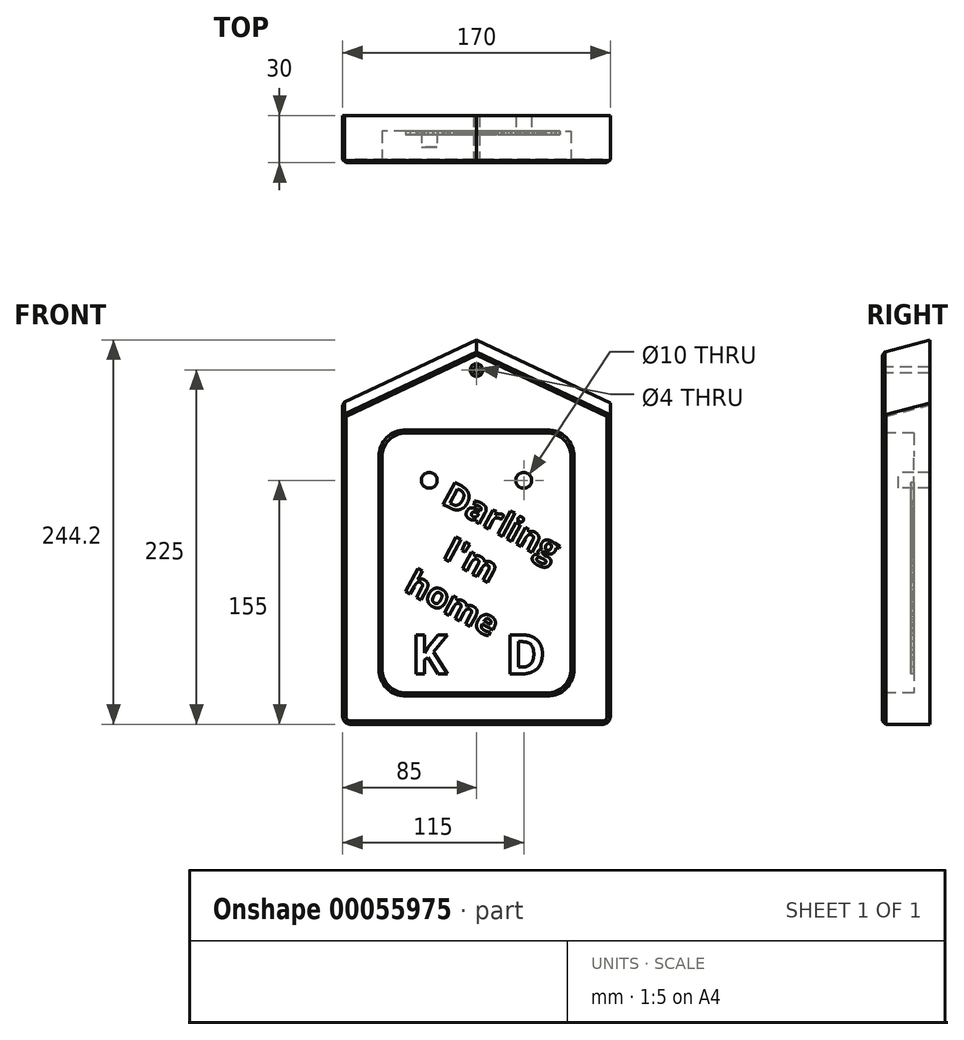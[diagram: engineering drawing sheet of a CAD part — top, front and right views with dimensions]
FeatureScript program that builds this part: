
annotation { "Feature Type Name" : "Feature", "Feature Type Description" : "" }
export const myFeature = defineFeature(function(context is Context, id is Id, definition is map)
    precondition{}
    {
        {
            var Q0;
            Q0=qCreatedBy(makeId("Front.planeOp"),FACE);
            var sketch = newSketch(context, id + "F0", { "sketchPlane" : qUnion([Q0])});
            skLineSegment(sketch, "E0.rect.bottom", {"start": v(45, -82.5) * mm, "end": v(-45, -82.5) * mm});
            skLineSegment(sketch, "E0.rect.top", {"start": v(45, 82.5) * mm, "end": v(-45, 82.5) * mm});
            skLineSegment(sketch, "E0.rect.left", {"start": v(60, -67.5) * mm, "end": v(60, 67.5) * mm});
            skLineSegment(sketch, "E0.rect.right", {"start": v(-60, -67.5) * mm, "end": v(-60, 67.5) * mm});
            skPoint(sketch, "E0.rect.middle", {"position": v(0, 0) * mm});
            skCircle(sketch, "E1", {"center": v(-30, 52.5) * mm, "radius": 5 * mm});
            skCircle(sketch, "E2.MirrorC", {"center": v(30, 52.5) * mm, "radius": 5 * mm});
            skPoint(sketch, "E3.visualSharp", {"position": v(60, 82.5) * mm});
            skArc(sketch, "E3.filletArc", {"start": v(60, 67.5) * mm, "mid": v(55.6, 78.1) * mm, "end": v(45, 82.5) * mm});
            skPoint(sketch, "E4.visualSharp", {"position": v(-60, 82.5) * mm});
            skArc(sketch, "E4.filletArc", {"start": v(-45, 82.5) * mm, "mid": v(-55.6, 78.1) * mm, "end": v(-60, 67.5) * mm});
            skPoint(sketch, "E5.visualSharp", {"position": v(-60, -82.5) * mm});
            skArc(sketch, "E5.filletArc", {"start": v(-60, -67.5) * mm, "mid": v(-55.6, -78.1) * mm, "end": v(-45, -82.5) * mm});
            skPoint(sketch, "E6.visualSharp", {"position": v(60, -82.5) * mm});
            skArc(sketch, "E6.filletArc", {"start": v(45, -82.5) * mm, "mid": v(55.6, -78.1) * mm, "end": v(60, -67.5) * mm});
            skLineSegment(sketch, "E7.rect.bottom", {"start": v(0, -102.5) * mm, "end": v(-80, -102.5) * mm});
            skLineSegment(sketch, "E7.rect.top", {"start": v(0, 142.5) * mm, "end": v(-85, 102.5) * mm});
            skLineSegment(sketch, "E7.rect.right", {"start": v(-85, -97.5) * mm, "end": v(-85, 102.5) * mm});
            skText(sketch, "E8", { "text": "K", "fontName": "OpenSans-Bold.ttf"});
            skText(sketch, "E9", { "text": "D", "fontName": "OpenSans-Bold.ttf"});
            skPoint(sketch, "E10.startSnap0", {"position": v(0, 142.5) * mm});
            skPoint(sketch, "E10.endSnap0", {"position": v(0, -82.5) * mm});
            skText(sketch, "E11", { "text": "Darling\n   I\'m\n home", "fontName": "OpenSans-Bold.ttf"});
            skPoint(sketch, "E12.visualSharp", {"position": v(-85, -102.5) * mm});
            skArc(sketch, "E12.filletArc", {"start": v(-85, -97.5) * mm, "mid": v(-83.54, -101.04) * mm, "end": v(-80, -102.5) * mm});
            skCircle(sketch, "E13", {"center": v(0, 122.5) * mm, "radius": 2 * mm});
            skPoint(sketch, "E14.MirrorCS.start.orphan", {"position": v(0, -102.5) * mm});
            skLineSegment(sketch, "E15", {"start": v(0, 105.13) * mm, "end": v(0, -95.47) * mm, "construction": true});
            skLineSegment(sketch, "E16.MirrorCS", {"start": v(0, 142.5) * mm, "end": v(85, 102.5) * mm});
            skLineSegment(sketch, "E17.MirrorCS", {"start": v(85, -97.5) * mm, "end": v(85, 102.5) * mm});
            skArc(sketch, "E18.MirrorCS", {"start": v(85, -97.5) * mm, "mid": v(83.54, -101.04) * mm, "end": v(80, -102.5) * mm});
            skLineSegment(sketch, "E19.MirrorCS", {"start": v(0, -102.5) * mm, "end": v(80, -102.5) * mm});
            const initialGuessF0  = {"E8": [-0.04153, -0.0705, 1, 0, 0.025], "E9": [0.01816, -0.0705, 1, 0, 0.025], "E11": [-0.02296, 0.03819, 0.87871, -0.47735, 0.01592]};
            skSetInitialGuess(sketch, initialGuessF0);
            skSolve(sketch);
        }
        {
            var Q0;
            Q0=makeQuery(id+"F0.imprint","IMPRINT",FACE,{"disambiguationData":[TD([[makeQuery(id+"F0.imprint","IMPRINT",EDGE,{"derivedFrom":sQuery(id+"F0.wireOp",EDGE,"E0.rect.bottom")}),1.0]])]});
            var Q1;
            Q1=makeQuery(id+"F0.imprint","IMPRINT",FACE,{"disambiguationData":[TD([[makeQuery(id+"F0.imprint","IMPRINT",EDGE,{"derivedFrom":sQuery(id+"F0.wireOp",EDGE,"E0.rect.bottom")}),-1.0]])]});
            var Q2;
            Q2 = qSketchRegion(id + "F0", true);
            var Q3;
            Q3=makeQuery(id+"F0.imprint","IMPRINT",FACE,{"disambiguationData":[TD([[makeQuery(id+"F0.imprint","IMPRINT",EDGE,{"derivedFrom":sQuery(id+"F0.wireOp",EDGE,"E11.sketch_text.stroke-160")}),-1.0]])]});
            var Q4;
            Q4=makeQuery(id+"F0.imprint","IMPRINT",FACE,{"disambiguationData":[TD([[makeQuery(id+"F0.imprint","IMPRINT",EDGE,{"derivedFrom":sQuery(id+"F0.wireOp",EDGE,"E1")}),1.0]])]});
            var Q5;
            Q5=makeQuery(id+"F0.imprint","IMPRINT",FACE,{"disambiguationData":[TD([[makeQuery(id+"F0.imprint","IMPRINT",EDGE,{"derivedFrom":sQuery(id+"F0.wireOp",EDGE,"E2.MirrorC")}),-1.0]])]});
            var Q6;
            Q6=makeQuery(id+"F0.imprint","IMPRINT",FACE,{"disambiguationData":[TD([[makeQuery(id+"F0.imprint","IMPRINT",EDGE,{"derivedFrom":sQuery(id+"F0.wireOp",EDGE,"E8.sketch_text.stroke-0")}),-1.0]])]});
            var Q7;
            Q7=makeQuery(id+"F0.imprint","IMPRINT",FACE,{"disambiguationData":[TD([[makeQuery(id+"F0.imprint","IMPRINT",EDGE,{"derivedFrom":sQuery(id+"F0.wireOp",EDGE,"E9.sketch_text.stroke-7")}),1.0]])]});
            var Q8;
            Q8=makeQuery(id+"F0.imprint","IMPRINT",FACE,{"disambiguationData":[TD([[makeQuery(id+"F0.imprint","IMPRINT",EDGE,{"derivedFrom":sQuery(id+"F0.wireOp",EDGE,"E11.sketch_text.stroke-7")}),1.0]])]});
            var Q9;
            Q9=makeQuery(id+"F0.imprint","IMPRINT",FACE,{"disambiguationData":[TD([[makeQuery(id+"F0.imprint","IMPRINT",EDGE,{"derivedFrom":sQuery(id+"F0.wireOp",EDGE,"E11.sketch_text.stroke-30")}),1.0]])]});
            var Q10;
            Q10=makeQuery(id+"F0.imprint","IMPRINT",FACE,{"disambiguationData":[TD([[makeQuery(id+"F0.imprint","IMPRINT",EDGE,{"derivedFrom":sQuery(id+"F0.wireOp",EDGE,"E11.sketch_text.stroke-223")}),1.0]])]});
            var Q11;
            Q11=makeQuery(id+"F0.imprint","IMPRINT",FACE,{"disambiguationData":[TD([[makeQuery(id+"F0.imprint","IMPRINT",EDGE,{"derivedFrom":sQuery(id+"F0.wireOp",EDGE,"E11.sketch_text.stroke-195")}),-1.0]])]});
            var Q12;
            Q12=makeQuery(id+"F0.imprint","IMPRINT",FACE,{"disambiguationData":[TD([[makeQuery(id+"F0.imprint","IMPRINT",EDGE,{"derivedFrom":sQuery(id+"F0.wireOp",EDGE,"E11.sketch_text.stroke-223")}),-1.0]])]});
            var Q13;
            Q13=makeQuery(id+"F0.imprint","IMPRINT",FACE,{"disambiguationData":[TD([[makeQuery(id+"F0.imprint","IMPRINT",EDGE,{"derivedFrom":sQuery(id+"F0.wireOp",EDGE,"E11.sketch_text.stroke-63")}),-1.0]])]});
            var Q14;
            Q14=makeQuery(id+"F0.imprint","IMPRINT",FACE,{"disambiguationData":[TD([[makeQuery(id+"F0.imprint","IMPRINT",EDGE,{"derivedFrom":sQuery(id+"F0.wireOp",EDGE,"E11.sketch_text.stroke-0")}),-1.0]])]});
            var Q15;
            Q15=makeQuery(id+"F0.imprint","IMPRINT",FACE,{"disambiguationData":[TD([[makeQuery(id+"F0.imprint","IMPRINT",EDGE,{"derivedFrom":sQuery(id+"F0.wireOp",EDGE,"E11.sketch_text.stroke-37")}),-1.0]])]});
            var Q16;
            Q16=makeQuery(id+"F0.imprint","IMPRINT",FACE,{"disambiguationData":[TD([[makeQuery(id+"F0.imprint","IMPRINT",EDGE,{"derivedFrom":sQuery(id+"F0.wireOp",EDGE,"E11.sketch_text.stroke-118")}),1.0]])]});
            var Q17;
            Q17=makeQuery(id+"F0.imprint","IMPRINT",FACE,{"disambiguationData":[TD([[makeQuery(id+"F0.imprint","IMPRINT",EDGE,{"derivedFrom":sQuery(id+"F0.wireOp",EDGE,"E11.sketch_text.stroke-12")}),-1.0]])]});
            var Q18;
            Q18=makeQuery(id+"F0.imprint","IMPRINT",FACE,{"disambiguationData":[TD([[makeQuery(id+"F0.imprint","IMPRINT",EDGE,{"derivedFrom":sQuery(id+"F0.wireOp",EDGE,"E11.sketch_text.stroke-59")}),-1.0]])]});
            var Q19;
            Q19=makeQuery(id+"F0.imprint","IMPRINT",FACE,{"disambiguationData":[TD([[makeQuery(id+"F0.imprint","IMPRINT",EDGE,{"derivedFrom":sQuery(id+"F0.wireOp",EDGE,"E9.sketch_text.stroke-0")}),-1.0]])]});
            var Q20;
            Q20=makeQuery(id+"F0.imprint","IMPRINT",FACE,{"disambiguationData":[TD([[makeQuery(id+"F0.imprint","IMPRINT",EDGE,{"derivedFrom":sQuery(id+"F0.wireOp",EDGE,"E11.sketch_text.stroke-50")}),-1.0]])]});
            var Q21;
            Q21=makeQuery(id+"F0.imprint","IMPRINT",FACE,{"disambiguationData":[TD([[makeQuery(id+"F0.imprint","IMPRINT",EDGE,{"derivedFrom":sQuery(id+"F0.wireOp",EDGE,"E11.sketch_text.stroke-132")}),-1.0]])]});
            var Q22;
            Q22=makeQuery(id+"F0.imprint","IMPRINT",FACE,{"disambiguationData":[TD([[makeQuery(id+"F0.imprint","IMPRINT",EDGE,{"derivedFrom":sQuery(id+"F0.wireOp",EDGE,"E11.sketch_text.stroke-124")}),-1.0]])]});
            var Q23;
            Q23=makeQuery(id+"F0.imprint","IMPRINT",FACE,{"disambiguationData":[TD([[makeQuery(id+"F0.imprint","IMPRINT",EDGE,{"derivedFrom":sQuery(id+"F0.wireOp",EDGE,"E11.sketch_text.stroke-128")}),-1.0]])]});
            var Q24;
            Q24=makeQuery(id+"F0.imprint","IMPRINT",FACE,{"disambiguationData":[TD([[makeQuery(id+"F0.imprint","IMPRINT",EDGE,{"derivedFrom":sQuery(id+"F0.wireOp",EDGE,"E11.sketch_text.stroke-177")}),1.0]])]});
            var Q25;
            Q25=makeQuery(id+"F0.imprint","IMPRINT",FACE,{"disambiguationData":[TD([[makeQuery(id+"F0.imprint","IMPRINT",EDGE,{"derivedFrom":sQuery(id+"F0.wireOp",EDGE,"E11.sketch_text.stroke-177")}),-1.0]])]});
            var Q26;
            Q26=makeQuery(id+"F0.imprint","IMPRINT",FACE,{"disambiguationData":[TD([[makeQuery(id+"F0.imprint","IMPRINT",EDGE,{"derivedFrom":sQuery(id+"F0.wireOp",EDGE,"E11.sketch_text.stroke-80")}),-1.0]])]});
            var Q27;
            Q27=makeQuery(id+"F0.imprint","IMPRINT",FACE,{"disambiguationData":[TD([[makeQuery(id+"F0.imprint","IMPRINT",EDGE,{"derivedFrom":sQuery(id+"F0.wireOp",EDGE,"E11.sketch_text.stroke-109")}),1.0]])]});
            var Q28;
            Q28=makeQuery(id+"F0.imprint","IMPRINT",FACE,{"disambiguationData":[TD([[makeQuery(id+"F0.imprint","IMPRINT",EDGE,{"derivedFrom":sQuery(id+"F0.wireOp",EDGE,"E11.sketch_text.stroke-54")}),-1.0]])]});
            extrude(context, id + "F1", {"entities" : qUnion([Q0, Q1, Q2, Q3, Q4, Q5, Q6, Q7, Q8, Q9, Q10, Q11, Q12, Q13, Q14, Q15, Q16, Q17, Q18, Q19, Q20, Q21, Q22, Q23, Q24, Q25, Q26, Q27, Q28]), "oppositeDirection" : true, "depth" : 30 * mm});
        }
        {
            var Q0;
            Q0=makeQuery(id+"F0.imprint","IMPRINT",FACE,{"disambiguationData":[TD([[makeQuery(id+"F0.imprint","IMPRINT",EDGE,{"derivedFrom":sQuery(id+"F0.wireOp",EDGE,"E0.rect.bottom")}),-1.0]])]});
            var Q1;
            Q1=makeQuery(id+"F0.imprint","IMPRINT",FACE,{"disambiguationData":[TD([[makeQuery(id+"F0.imprint","IMPRINT",EDGE,{"derivedFrom":sQuery(id+"F0.wireOp",EDGE,"E11.sketch_text.stroke-7")}),1.0]])]});
            var Q2;
            Q2=makeQuery(id+"F0.imprint","IMPRINT",FACE,{"disambiguationData":[TD([[makeQuery(id+"F0.imprint","IMPRINT",EDGE,{"derivedFrom":sQuery(id+"F0.wireOp",EDGE,"E11.sketch_text.stroke-177")}),1.0]])]});
            var Q3;
            Q3=makeQuery(id+"F0.imprint","IMPRINT",FACE,{"disambiguationData":[TD([[makeQuery(id+"F0.imprint","IMPRINT",EDGE,{"derivedFrom":sQuery(id+"F0.wireOp",EDGE,"E9.sketch_text.stroke-7")}),1.0]])]});
            var Q4;
            Q4=makeQuery(id+"F0.imprint","IMPRINT",FACE,{"disambiguationData":[TD([[makeQuery(id+"F0.imprint","IMPRINT",EDGE,{"derivedFrom":sQuery(id+"F0.wireOp",EDGE,"E11.sketch_text.stroke-118")}),1.0]])]});
            var Q5;
            Q5=makeQuery(id+"F0.imprint","IMPRINT",FACE,{"disambiguationData":[TD([[makeQuery(id+"F0.imprint","IMPRINT",EDGE,{"derivedFrom":sQuery(id+"F0.wireOp",EDGE,"E11.sketch_text.stroke-109")}),1.0]])]});
            var Q6;
            Q6=makeQuery(id+"F0.imprint","IMPRINT",FACE,{"disambiguationData":[TD([[makeQuery(id+"F0.imprint","IMPRINT",EDGE,{"derivedFrom":sQuery(id+"F0.wireOp",EDGE,"E11.sketch_text.stroke-223")}),1.0]])]});
            var Q7;
            Q7=makeQuery(id+"F0.imprint","IMPRINT",FACE,{"disambiguationData":[TD([[makeQuery(id+"F0.imprint","IMPRINT",EDGE,{"derivedFrom":sQuery(id+"F0.wireOp",EDGE,"E11.sketch_text.stroke-30")}),1.0]])]});
            extrude(context, id + "F2", {"entities" : qUnion([Q0, Q1, Q2, Q3, Q4, Q5, Q6, Q7]), "operationType" : NewBodyOperationType.REMOVE, "oppositeDirection" : true, "depth" : 20 * mm});
        }
        {
            var Q0;
            Q0=makeQuery(id+"F0.imprint","IMPRINT",FACE,{"disambiguationData":[TD([[makeQuery(id+"F0.imprint","IMPRINT",EDGE,{"derivedFrom":sQuery(id+"F0.wireOp",EDGE,"E8.sketch_text.stroke-0")}),-1.0]])]});
            var Q1;
            Q1=makeQuery(id+"F0.imprint","IMPRINT",FACE,{"disambiguationData":[TD([[makeQuery(id+"F0.imprint","IMPRINT",EDGE,{"derivedFrom":sQuery(id+"F0.wireOp",EDGE,"E9.sketch_text.stroke-0")}),-1.0]])]});
            var Q2;
            Q2=makeQuery(id+"F0.imprint","IMPRINT",FACE,{"disambiguationData":[TD([[makeQuery(id+"F0.imprint","IMPRINT",EDGE,{"derivedFrom":sQuery(id+"F0.wireOp",EDGE,"E11.sketch_text.stroke-223")}),-1.0]])]});
            var Q3;
            Q3=makeQuery(id+"F0.imprint","IMPRINT",FACE,{"disambiguationData":[TD([[makeQuery(id+"F0.imprint","IMPRINT",EDGE,{"derivedFrom":sQuery(id+"F0.wireOp",EDGE,"E11.sketch_text.stroke-195")}),-1.0]])]});
            var Q4;
            Q4=makeQuery(id+"F0.imprint","IMPRINT",FACE,{"disambiguationData":[TD([[makeQuery(id+"F0.imprint","IMPRINT",EDGE,{"derivedFrom":sQuery(id+"F0.wireOp",EDGE,"E11.sketch_text.stroke-177")}),-1.0]])]});
            var Q5;
            Q5=makeQuery(id+"F0.imprint","IMPRINT",FACE,{"disambiguationData":[TD([[makeQuery(id+"F0.imprint","IMPRINT",EDGE,{"derivedFrom":sQuery(id+"F0.wireOp",EDGE,"E11.sketch_text.stroke-160")}),-1.0]])]});
            var Q6;
            Q6=makeQuery(id+"F0.imprint","IMPRINT",FACE,{"disambiguationData":[TD([[makeQuery(id+"F0.imprint","IMPRINT",EDGE,{"derivedFrom":sQuery(id+"F0.wireOp",EDGE,"E11.sketch_text.stroke-124")}),-1.0]])]});
            var Q7;
            Q7=makeQuery(id+"F0.imprint","IMPRINT",FACE,{"disambiguationData":[TD([[makeQuery(id+"F0.imprint","IMPRINT",EDGE,{"derivedFrom":sQuery(id+"F0.wireOp",EDGE,"E11.sketch_text.stroke-128")}),-1.0]])]});
            var Q8;
            Q8=makeQuery(id+"F0.imprint","IMPRINT",FACE,{"disambiguationData":[TD([[makeQuery(id+"F0.imprint","IMPRINT",EDGE,{"derivedFrom":sQuery(id+"F0.wireOp",EDGE,"E11.sketch_text.stroke-132")}),-1.0]])]});
            var Q9;
            Q9=makeQuery(id+"F0.imprint","IMPRINT",FACE,{"disambiguationData":[TD([[makeQuery(id+"F0.imprint","IMPRINT",EDGE,{"derivedFrom":sQuery(id+"F0.wireOp",EDGE,"E11.sketch_text.stroke-0")}),-1.0]])]});
            var Q10;
            Q10=makeQuery(id+"F0.imprint","IMPRINT",FACE,{"disambiguationData":[TD([[makeQuery(id+"F0.imprint","IMPRINT",EDGE,{"derivedFrom":sQuery(id+"F0.wireOp",EDGE,"E11.sketch_text.stroke-12")}),-1.0]])]});
            var Q11;
            Q11=makeQuery(id+"F0.imprint","IMPRINT",FACE,{"disambiguationData":[TD([[makeQuery(id+"F0.imprint","IMPRINT",EDGE,{"derivedFrom":sQuery(id+"F0.wireOp",EDGE,"E11.sketch_text.stroke-37")}),-1.0]])]});
            var Q12;
            Q12=makeQuery(id+"F0.imprint","IMPRINT",FACE,{"disambiguationData":[TD([[makeQuery(id+"F0.imprint","IMPRINT",EDGE,{"derivedFrom":sQuery(id+"F0.wireOp",EDGE,"E11.sketch_text.stroke-50")}),-1.0]])]});
            var Q13;
            Q13=makeQuery(id+"F0.imprint","IMPRINT",FACE,{"disambiguationData":[TD([[makeQuery(id+"F0.imprint","IMPRINT",EDGE,{"derivedFrom":sQuery(id+"F0.wireOp",EDGE,"E11.sketch_text.stroke-59")}),-1.0]])]});
            var Q14;
            Q14=makeQuery(id+"F0.imprint","IMPRINT",FACE,{"disambiguationData":[TD([[makeQuery(id+"F0.imprint","IMPRINT",EDGE,{"derivedFrom":sQuery(id+"F0.wireOp",EDGE,"E11.sketch_text.stroke-54")}),-1.0]])]});
            var Q15;
            Q15=makeQuery(id+"F0.imprint","IMPRINT",FACE,{"disambiguationData":[TD([[makeQuery(id+"F0.imprint","IMPRINT",EDGE,{"derivedFrom":sQuery(id+"F0.wireOp",EDGE,"E11.sketch_text.stroke-63")}),-1.0]])]});
            var Q16;
            Q16=makeQuery(id+"F0.imprint","IMPRINT",FACE,{"disambiguationData":[TD([[makeQuery(id+"F0.imprint","IMPRINT",EDGE,{"derivedFrom":sQuery(id+"F0.wireOp",EDGE,"E11.sketch_text.stroke-80")}),-1.0]])]});
            extrude(context, id + "F3", {"entities" : qUnion([Q0, Q1, Q2, Q3, Q4, Q5, Q6, Q7, Q8, Q9, Q10, Q11, Q12, Q13, Q14, Q15, Q16]), "operationType" : NewBodyOperationType.REMOVE, "oppositeDirection" : true, "depth" : 18 * mm});
        }
        {
            var Q0;
            Q0=makeQuery(id+"F0.imprint","IMPRINT",FACE,{"disambiguationData":[TD([[makeQuery(id+"F0.imprint","IMPRINT",EDGE,{"derivedFrom":sQuery(id+"F0.wireOp",EDGE,"E1")}),1.0]])]});
            var Q1;
            Q1=makeQuery(id+"F0.imprint","IMPRINT",FACE,{"disambiguationData":[TD([[makeQuery(id+"F0.imprint","IMPRINT",EDGE,{"derivedFrom":sQuery(id+"F0.wireOp",EDGE,"E2.MirrorC")}),-1.0]])]});
            extrude(context, id + "F4", {"entities" : qUnion([Q0, Q1]), "operationType" : NewBodyOperationType.REMOVE, "oppositeDirection" : true, "depth" : 10 * mm});
        }
        {
            var Q0;
            Q0=makeQuery(id+"F1.opExtrude","CAP_EDGE",EDGE,{"disambiguationData":[OSD([sQuery(id+"F0.wireOp",EDGE,"E7.rect.top")])],"isStart":true});
            var Q1;
            Q1=makeQuery(id+"F1.opExtrude","CAP_EDGE",EDGE,{"disambiguationData":[OSD([sQuery(id+"F0.wireOp",EDGE,"E16.MirrorCS")])],"isStart":true});
            chamfer(context, id + "F5", {"entities" : qUnion([Q0, Q1]), "chamferType" : ChamferType.TWO_OFFSETS, "width1" : 33 * mm, "oppositeDirection" : true, "width2" : 8 * mm});
        }
        {
            var Q0;
            {var subQ0=sQuery(id+"F0.wireOp",EDGE,"E13");var subQ1=sQuery(id+"F0.wireOp",EDGE,"f0fe2e16-c990-476e-b693-ec943d4486760.MirrorCS");var subQ2=sQuery(id+"F0.wireOp",EDGE,"01861193-d176-493b-b0e6-384450b6c0f20.MirrorCS");var subQ3=sQuery(id+"F0.wireOp",EDGE,"186c9093-d3af-4f1b-87e9-1d0e739dd6b90.MirrorCS");var subQ4=sQuery(id+"F0.wireOp",EDGE,"E14.MirrorCS");var subQ5=sQuery(id+"F0.wireOp",EDGE,"E7.rect.bottom");var subQ6=sQuery(id+"F0.wireOp",EDGE,"E7.rect.top");var subQ7=sQuery(id+"F0.wireOp",EDGE,"E7.rect.right");var subQ8=sQuery(id+"F0.wireOp",EDGE,"E12.filletArc");Q0=makeQuery(id+"F2.boolean.opBoolean","SPLIT",FACE,{"disambiguationData":[TD([makeQuery(id+"F1.opExtrude","SWEPT_FACE",FACE,{"disambiguationData":[OSD([subQ6])]})])],"derivedFrom":makeQuery(id+"F1.opExtrude","CAP_FACE",FACE,{"disambiguationData":[OSD([subQ5,subQ6,subQ7,subQ8,subQ3,subQ2,subQ4,subQ1,subQ0])],"isStart":true})});}
            var Q1;
            Q1=makeQuery(id+"F5.opChamfer","BLEND_EDGE",EDGE,{"blendedFrom":[makeQuery(id+"F1.opExtrude","CAP_EDGE",EDGE,{"disambiguationData":[OSD([sQuery(id+"F0.wireOp",EDGE,"186c9093-d3af-4f1b-87e9-1d0e739dd6b90.MirrorCS")])],"isStart":true}),makeQuery(id+"F1.opExtrude","SWEPT_FACE",FACE,{"disambiguationData":[OSD([sQuery(id+"F0.wireOp",EDGE,"01861193-d176-493b-b0e6-384450b6c0f20.MirrorCS")])]})],"blendedInto":[makeQuery(id+"F1.opExtrude","SWEPT_FACE",FACE,{"disambiguationData":[OSD([sQuery(id+"F0.wireOp",EDGE,"01861193-d176-493b-b0e6-384450b6c0f20.MirrorCS")])]})]});
            var Q2;
            Q2=makeQuery(id+"F5.opChamfer","BLEND_EDGE",EDGE,{"blendedFrom":[makeQuery(id+"F1.opExtrude","CAP_EDGE",EDGE,{"disambiguationData":[OSD([sQuery(id+"F0.wireOp",EDGE,"E7.rect.top")])],"isStart":true}),makeQuery(id+"F1.opExtrude","SWEPT_FACE",FACE,{"disambiguationData":[OSD([sQuery(id+"F0.wireOp",EDGE,"E7.rect.right")])]})],"blendedInto":[makeQuery(id+"F1.opExtrude","SWEPT_FACE",FACE,{"disambiguationData":[OSD([sQuery(id+"F0.wireOp",EDGE,"E7.rect.right")])]})]});
            chamfer(context, id + "F6", {"entities" : qUnion([Q0, Q1, Q2]), "width" : 2 * mm, "tangentPropagation" : true});
        }
        {
            var Q0;
            Q0=makeQuery(id+"F4.boolean.opBoolean","COPY",FACE,{"derivedFrom":makeQuery(id+"F4.opExtrude","CAP_FACE",FACE,{"disambiguationData":[OSD([sQuery(id+"F0.wireOp",EDGE,"E1")])],"isStart":false})});
            var sketch = newSketch(context, id + "F7", { "sketchPlane" : qUnion([Q0])});
            skCircle(sketch, "E20", {"center": v(-30, 52.5) * mm, "radius": 1.5 * mm});
            skSolve(sketch);
        }
        {
            var Q0;
            Q0=makeQuery(id+"F4.boolean.opBoolean","COPY",FACE,{"derivedFrom":makeQuery(id+"F4.opExtrude","CAP_FACE",FACE,{"disambiguationData":[OSD([sQuery(id+"F0.wireOp",EDGE,"E2.MirrorC")])],"isStart":false})});
            var sketch = newSketch(context, id + "F8", { "sketchPlane" : qUnion([Q0])});
            skCircle(sketch, "E21", {"center": v(30, 52.5) * mm, "radius": 1.5 * mm});
            skSolve(sketch);
        }
        {
            var Q0;
            Q0 = qSketchRegion(id + "F8", true);
            var Q1;
            Q1 = qSketchRegion(id + "F7", true);
            extrude(context, id + "F9", {"entities" : qUnion([Q0, Q1]), "operationType" : NewBodyOperationType.REMOVE, "oppositeDirection" : true, "depth" : 2 * mm, "hasDraft" : true, "draftAngle" : 45 * degree, "draftPullDirection" : true});
        }
    });
